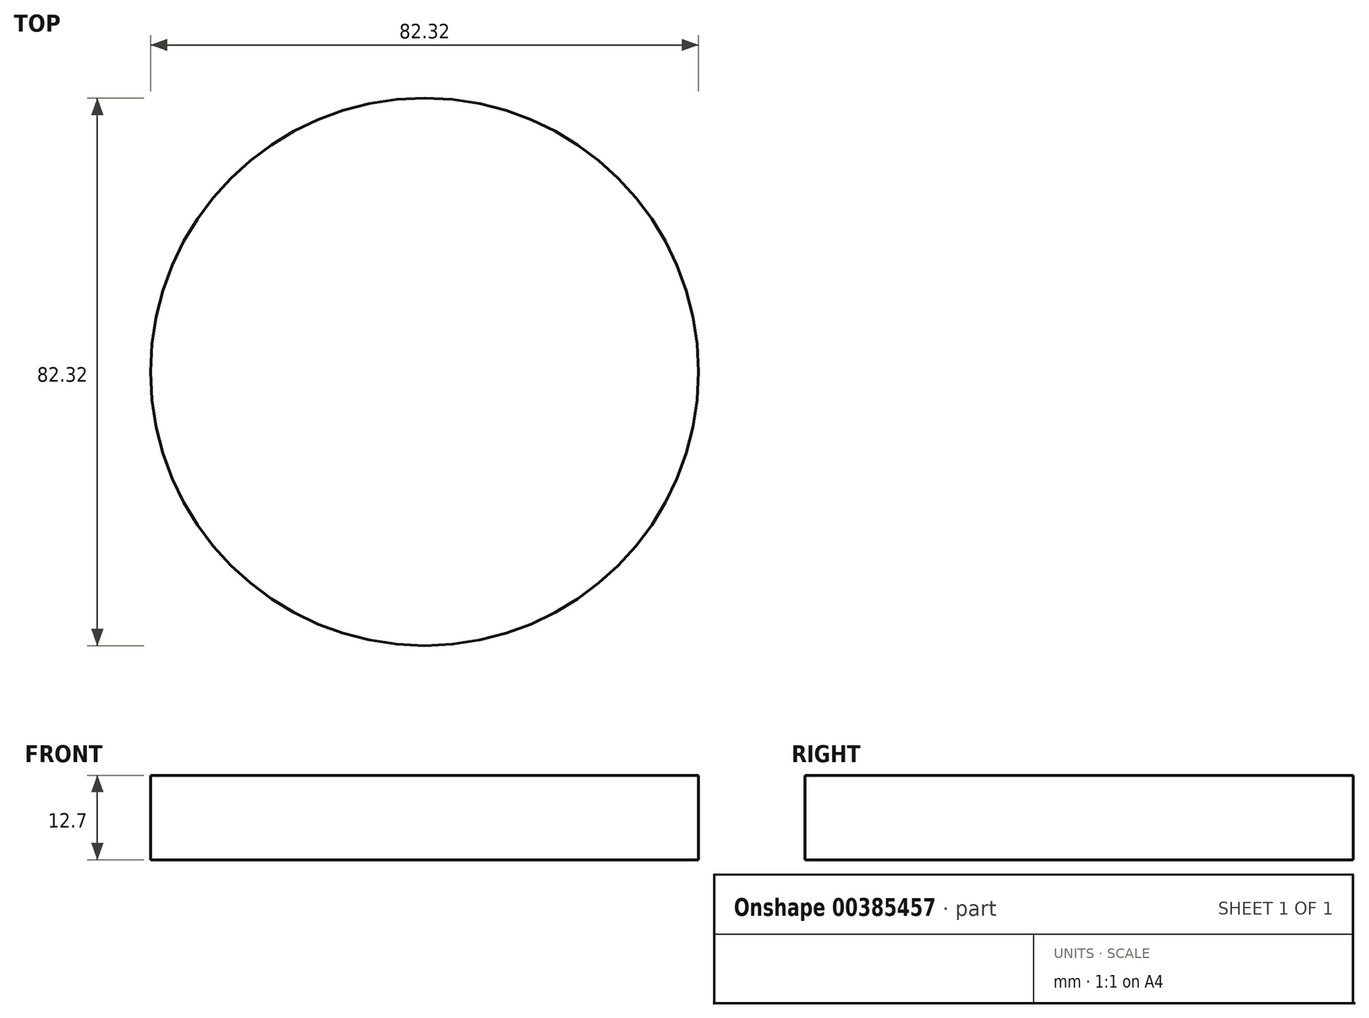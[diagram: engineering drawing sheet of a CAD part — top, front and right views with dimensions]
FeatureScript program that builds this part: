
annotation { "Feature Type Name" : "Feature", "Feature Type Description" : "" }
export const myFeature = defineFeature(function(context is Context, id is Id, definition is map)
    precondition{}
    {
        {
            var Q0;
            Q0=qCreatedBy(makeId("Top.planeOp"),FACE);
            var sketch = newSketch(context, id + "F0", { "sketchPlane" : qUnion([Q0])});
            skCircle(sketch, "E0", {"center": v(0, 0) * mm, "radius": 41.16 * mm});
            skSolve(sketch);
        }
        {
            var Q0;
            Q0=makeQuery(id+"F0.imprint","IMPRINT",FACE,{"disambiguationData":[TD([[makeQuery(id+"F0.imprint","IMPRINT",EDGE,{"derivedFrom":sQuery(id+"F0.wireOp",EDGE,"E0")}),1.0]])]});
            extrude(context, id + "F1", {"entities" : qUnion([Q0]), "depth" : 12.7 * mm});
        }
    });
